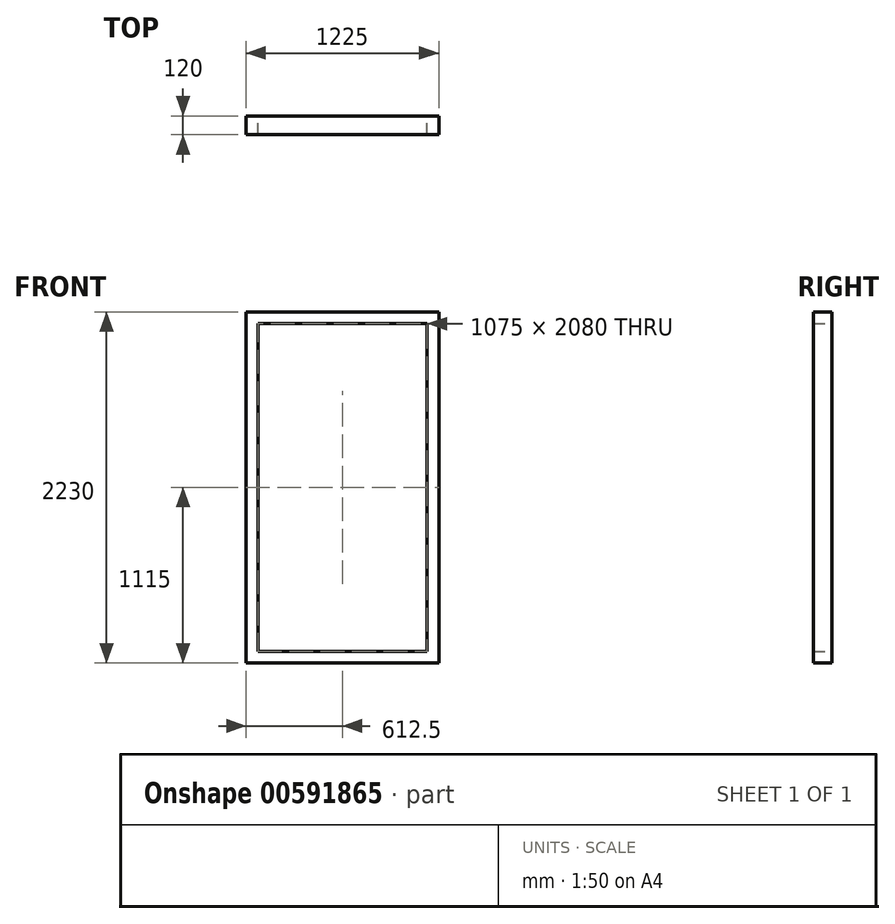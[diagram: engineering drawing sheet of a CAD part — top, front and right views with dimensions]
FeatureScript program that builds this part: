
annotation { "Feature Type Name" : "Feature", "Feature Type Description" : "" }
export const myFeature = defineFeature(function(context is Context, id is Id, definition is map)
    precondition{}
    {
        {
            var Q0;
            Q0=qCreatedBy(makeId("Front.planeOp"),FACE);
            var sketch = newSketch(context, id + "F0", { "sketchPlane" : qUnion([Q0])});
            skLineSegment(sketch, "E0.bottom", {"start": v(0, 0) * mm, "end": v(1225, 0) * mm});
            skLineSegment(sketch, "E0.top", {"start": v(0, 2230) * mm, "end": v(1225, 2230) * mm});
            skLineSegment(sketch, "E0.left", {"start": v(0, 0) * mm, "end": v(0, 2230) * mm});
            skLineSegment(sketch, "E0.right", {"start": v(1225, 0) * mm, "end": v(1225, 2230) * mm});
            skLineSegment(sketch, "E1.0", {"start": v(75, 2155) * mm, "end": v(1150, 2155) * mm});
            skLineSegment(sketch, "E1.1", {"start": v(75, 75) * mm, "end": v(75, 2155) * mm});
            skLineSegment(sketch, "E1.2", {"start": v(75, 75) * mm, "end": v(1150, 75) * mm});
            skLineSegment(sketch, "E1.3", {"start": v(1150, 75) * mm, "end": v(1150, 2155) * mm});
            skSolve(sketch);
        }
        {
            var Q0;
            Q0=qSketchRegion(id+"F0",true);
            extrude(context, id + "F1", {"entities" : qUnion([Q0]), "depth" : 120 * mm, "offsetDistance" : 25 * mm});
        }
    });
